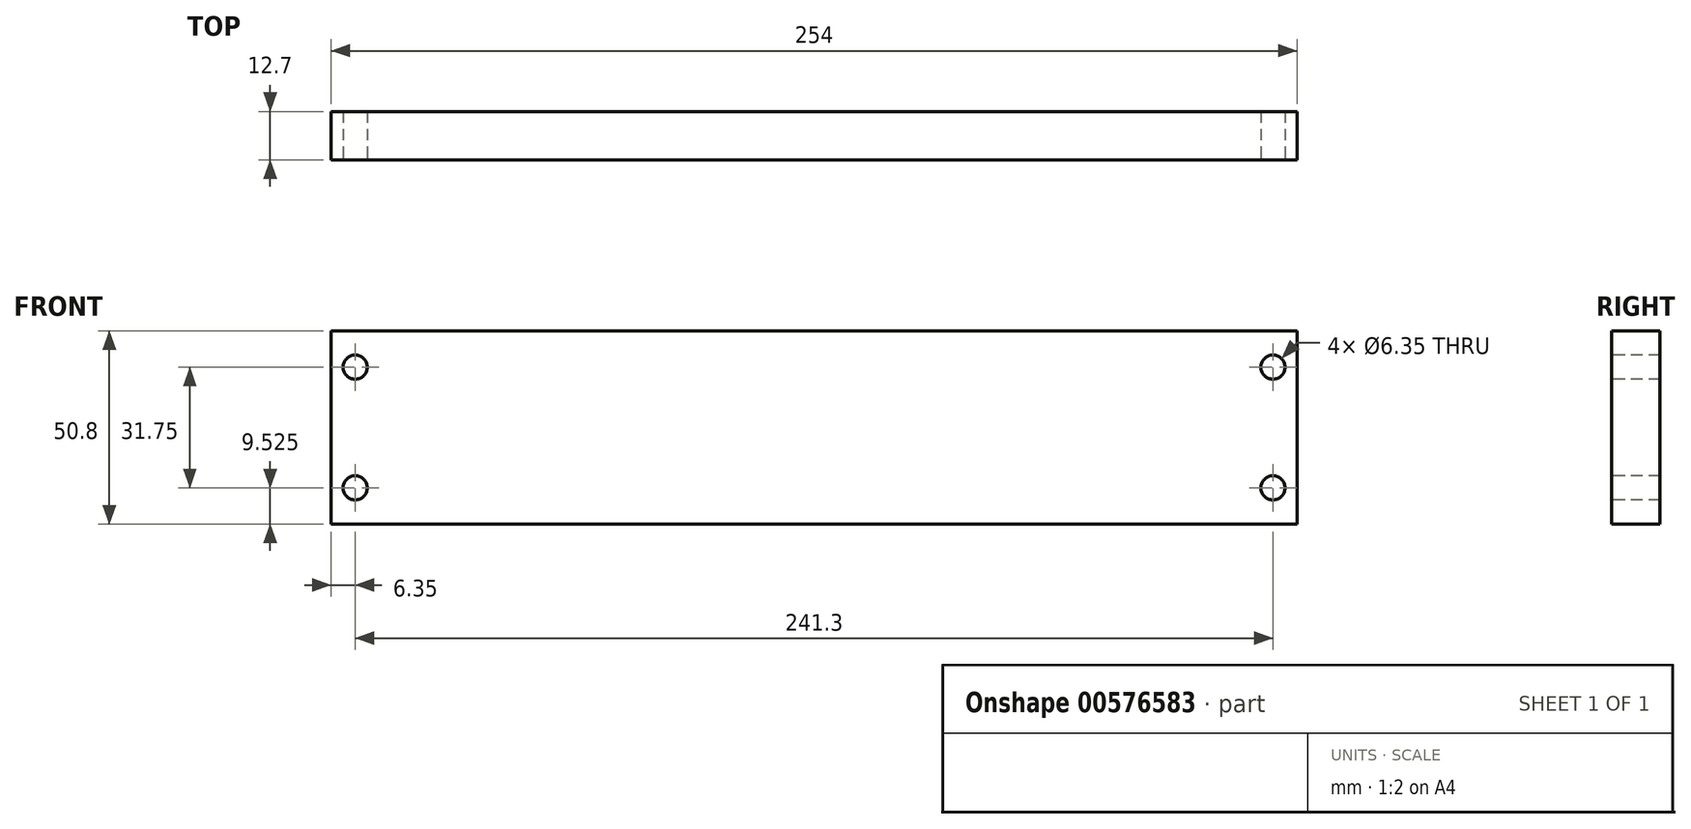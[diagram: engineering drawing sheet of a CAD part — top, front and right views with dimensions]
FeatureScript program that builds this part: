
annotation { "Feature Type Name" : "Feature", "Feature Type Description" : "" }
export const myFeature = defineFeature(function(context is Context, id is Id, definition is map)
    precondition{}
    {
        {
            var Q0;
            Q0=qCreatedBy(makeId("Front.planeOp"),FACE);
            var sketch = newSketch(context, id + "F0", { "sketchPlane" : qUnion([Q0])});
            skLineSegment(sketch, "E0.bottom", {"start": v(-127, 25.4) * mm, "end": v(127, 25.4) * mm});
            skLineSegment(sketch, "E0.top", {"start": v(-127, -25.4) * mm, "end": v(127, -25.4) * mm});
            skLineSegment(sketch, "E0.left", {"start": v(-127, 25.4) * mm, "end": v(-127, -25.4) * mm});
            skLineSegment(sketch, "E0.right", {"start": v(127, 25.4) * mm, "end": v(127, -25.4) * mm});
            skPoint(sketch, "E0.middle", {"position": v(0, 0) * mm});
            skPoint(sketch, "E1", {"position": v(-120.65, 15.87) * mm});
            skPoint(sketch, "E2.MirrorP", {"position": v(120.65, 15.87) * mm});
            skPoint(sketch, "E3.MirrorP", {"position": v(120.65, -15.87) * mm});
            skPoint(sketch, "E4.MirrorP", {"position": v(-120.65, -15.87) * mm});
            skSolve(sketch);
        }
        {
            var Q0;
            Q0=makeQuery(id+"F0.imprint","IMPRINT",FACE,{"disambiguationData":[TD([[makeQuery(id+"F0.imprint","IMPRINT",EDGE,{"derivedFrom":sQuery(id+"F0.wireOp",EDGE,"E0.bottom")}),-1.0]])]});
            extrude(context, id + "F1", {"entities" : qUnion([Q0]), "oppositeDirection" : true, "depth" : 12.7 * mm, "offsetDistance" : 25.4 * mm});
        }
        {
            var Q0;
            Q0=sQuery(id+"F0.wireOp",VERTEX,"E2.MirrorP");
            var Q1;
            Q1=sQuery(id+"F0.wireOp",VERTEX,"E3.MirrorP");
            var Q2;
            Q2=sQuery(id+"F0.wireOp",VERTEX,"E4.MirrorP");
            var Q3;
            Q3=sQuery(id+"F0.wireOp",VERTEX,"E1");
            var Q4;
            Q4=makeQuery(id+"F1.opExtrude","SWEPT_BODY",BODY,{"disambiguationData":[OSD([sQuery(id+"F0.wireOp",EDGE,"E0.bottom"),sQuery(id+"F0.wireOp",EDGE,"E0.top"),sQuery(id+"F0.wireOp",EDGE,"E0.left"),sQuery(id+"F0.wireOp",EDGE,"E0.right")])]});
            hole(context, id + "F2", {"style" : HoleStyle.SIMPLE, "endStyle" : HoleEndStyle.THROUGH, "holeDiameter" : 6.35 * mm, "isTappedThrough" : true, "tappedDepth" : 12.7 * mm, "tapClearance" : 3, "startFromSketch" : true, "locations" : qUnion([Q0, Q1, Q2, Q3]), "scope" : qUnion([Q4]), "majorDiameter" : 6.35 * mm});
        }
    });
